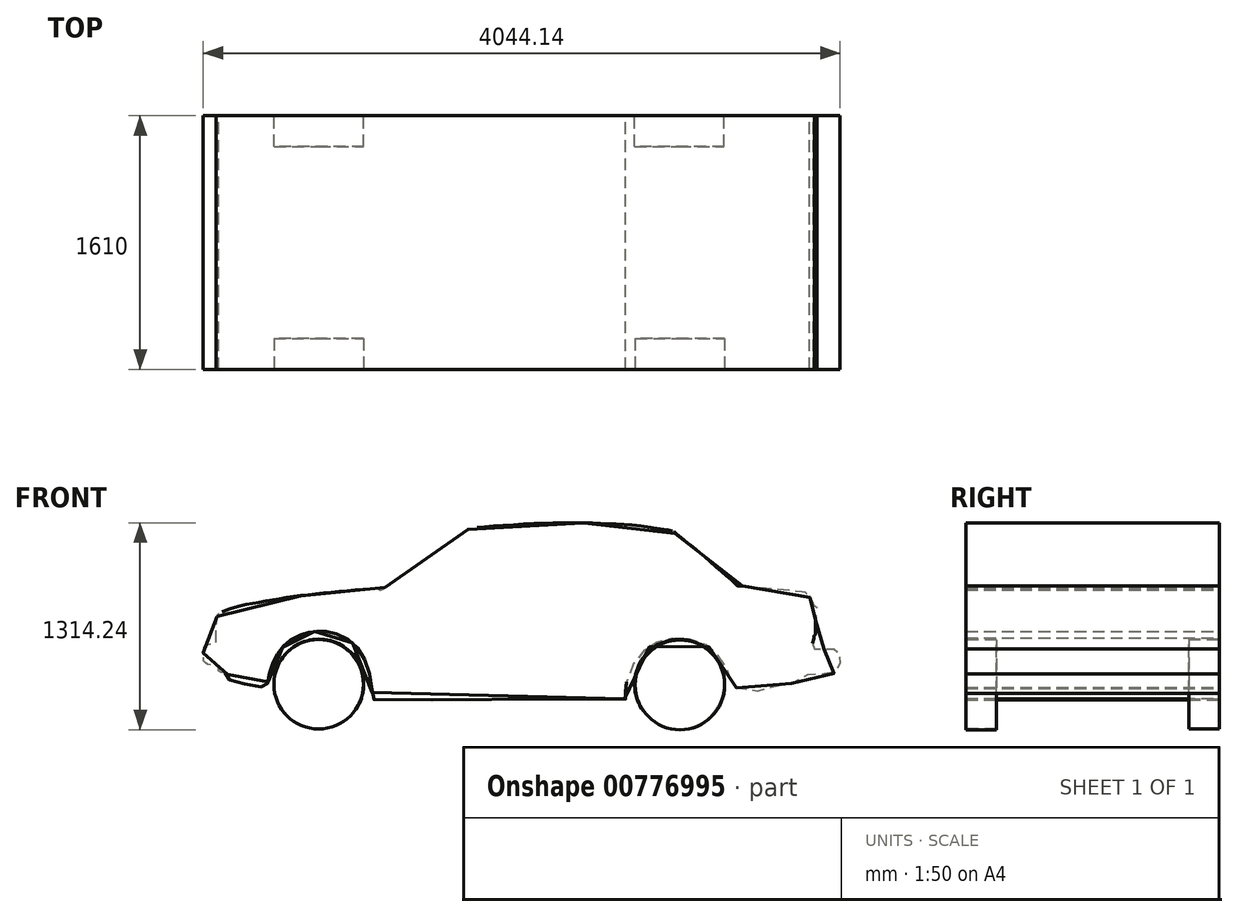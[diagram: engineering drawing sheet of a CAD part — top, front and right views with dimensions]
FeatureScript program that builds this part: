
annotation { "Feature Type Name" : "Feature", "Feature Type Description" : "" }
export const myFeature = defineFeature(function(context is Context, id is Id, definition is map)
    precondition{}
    {
        {
            var Q0;
            Q0=qCreatedBy(makeId("Front.planeOp"),FACE);
            var sketch = newSketch(context, id + "F0", { "sketchPlane" : qUnion([Q0])});
            skLineSegment(sketch, "E0", {"start": v(-4800.55, 868.38) * mm, "end": v(-4800.55, 1009.53) * mm, "construction": true});
            skFitSpline(sketch, "E1", {"points": [v(-2124.67, 593.9) * mm, v(-3714.16, 588.78) * mm, v(-3718.32, 591.35) * mm, v(-3722.74, 606.87) * mm, v(-3727.44, 630.77) * mm, v(-3729.78, 647.77) * mm, v(-3738.29, 703.5) * mm, v(-3747.23, 755.84) * mm, v(-3763.82, 814.56) * mm, v(-3776.59, 843.92) * mm, v(-3789.35, 869.45) * mm, v(-3814.84, 907.94) * mm, v(-3841.42, 938.45) * mm, v(-3867.01, 961.1) * mm, v(-3895.56, 980.78) * mm, v(-3929.03, 997.51) * mm, v(-3954.62, 1007.36) * mm, v(-3980.22, 1014.25) * mm, v(-4002.86, 1019.17) * mm, v(-4023.53, 1022.12) * mm, v(-4045.18, 1023.1) * mm, v(-4063.89, 1023.1) * mm, v(-4075.7, 1023.1) * mm, v(-4090.47, 1022.12) * mm, v(-4105.23, 1021.14) * mm, v(-4120.98, 1019.17) * mm, v(-4136.73, 1016.22) * mm, v(-4148.54, 1013.26) * mm, v(-4162.33, 1009.33) * mm, v(-4176.1, 1004.4) * mm, v(-4193.83, 997.51) * mm, v(-4213.51, 988.66) * mm, v(-4243.04, 969.95) * mm, v(-4260.76, 957.16) * mm, v(-4277.5, 943.37) * mm, v(-4292.26, 928.6) * mm, v(-4304.08, 915.81) * mm, v(-4313.92, 903.01) * mm, v(-4321.8, 891.2) * mm, v(-4332.62, 874.47) * mm, v(-4339.51, 862.66) * mm, v(-4349.36, 844.94) * mm, v(-4359.2, 821.31) * mm, v(-4368.06, 797.69) * mm, v(-4375.93, 773.08) * mm, v(-4382.82, 745.51) * mm, v(-4387.75, 720.9) * mm, v(-4390.7, 698.26) * mm, v(-4392.67, 688.42) * mm, v(-4398.57, 675.62) * mm, v(-4404.48, 667.75) * mm, v(-4433.03, 670.7) * mm, v(-4484.22, 677.6) * mm, v(-4554.1, 692.36) * mm, v(-4605.3, 705.16) * mm, v(-4635.8, 715) * mm, v(-4642.7, 725.83) * mm, v(-4647.62, 754.37) * mm, v(-4660.42, 758.31) * mm, v(-4688.97, 764.22) * mm, v(-4700.78, 771.1) * mm, v(-4705.7, 781.94) * mm, v(-4704.72, 794.73) * mm, v(-4704.72, 796.7) * mm, v(-4721.45, 801.62) * mm, v(-4772.64, 813.44) * mm, v(-4783.47, 821.31) * mm, v(-4796.26, 830.17) * mm, v(-4798.23, 841.98) * mm, v(-4801.18, 864.62) * mm, v(-4796.26, 923.69) * mm, v(-4787.4, 933.53) * mm, v(-4763.78, 941.4) * mm, v(-4743.1, 944.36) * mm, v(-4719.48, 946.33) * mm, v(-4719.48, 954.2) * mm, v(-4721.45, 998.5) * mm, v(-4720.47, 1046.73) * mm, v(-4715.54, 1097.92) * mm, v(-4713.58, 1111.7) * mm, v(-4709.64, 1128.44) * mm, v(-4700.78, 1138.28) * mm, v(-4671.25, 1152.06) * mm, v(-4597.42, 1177.66) * mm, v(-4447.8, 1208.17) * mm, v(-4272.57, 1237.7) * mm, v(-4066.84, 1263.3) * mm, v(-3832.56, 1285.94) * mm, v(-3697.7, 1295.78) * mm, v(-3693.76, 1295.78) * mm, v(-3687.86, 1292.83) * mm, v(-3681.95, 1288.89) * mm, v(-3674.07, 1284.95) * mm, v(-3670.14, 1285.94) * mm, v(-3642.57, 1306.6) * mm, v(-3377.78, 1492.66) * mm, v(-3153.34, 1646.22) * mm, v(-3148.42, 1649.17) * mm, v(-3144.48, 1653.1) * mm, v(-3136.6, 1658.03) * mm, v(-3134.64, 1661.97) * mm, v(-3133.65, 1666.89) * mm, v(-3129.72, 1669.84) * mm, v(-3119.87, 1670.83) * mm, v(-3088.37, 1677.72) * mm, v(-2891.5, 1696.42) * mm, v(-2592.25, 1711.19) * mm, v(-2398.32, 1712.17) * mm, v(-2216.22, 1706.26) * mm, v(-2008.51, 1690.51) * mm, v(-1824.43, 1661.97) * mm, v(-1816.56, 1660) * mm, v(-1808.68, 1657.05) * mm, v(-1806.71, 1653.1) * mm, v(-1804.75, 1651.14) * mm, v(-1803.76, 1646.22) * mm, v(-1799.82, 1644.25) * mm, v(-1757.5, 1611.76) * mm, v(-1633.47, 1511.36) * mm, v(-1434.62, 1338.1) * mm, v(-1411, 1315.47) * mm, v(-1409.03, 1311.53) * mm, v(-1403.12, 1311.53) * mm, v(-1346.03, 1307.6) * mm, v(-1275.15, 1301.69) * mm, v(-1117.65, 1289.87) * mm, v(-1028.07, 1280.03) * mm, v(-979.84, 1273.14) * mm, v(-976.89, 1270.19) * mm, v(-970, 1265.26) * mm, v(-950.3, 1241.64) * mm, v(-936.53, 1219) * mm, v(-925.7, 1195.37) * mm, v(-922.75, 1185.53) * mm, v(-916.84, 1184.55) * mm, v(-909.95, 1179.62) * mm, v(-904.04, 1172.73) * mm, v(-903.06, 1167.81) * mm, v(-904.04, 1160.92) * mm, v(-905.03, 1157.97) * mm, v(-907.98, 1153.05) * mm, v(-909.95, 1151.08) * mm, v(-912.9, 1147.14) * mm, v(-915.86, 1144.19) * mm, v(-919.8, 1140.25) * mm, v(-919.8, 1135.33) * mm, v(-914.87, 1125.48) * mm, v(-914.87, 1117.6) * mm, v(-913.89, 1105.8) * mm, v(-912.9, 1083.16) * mm, v(-912.9, 1051.66) * mm, v(-913.89, 1026.06) * mm, v(-915.86, 999.48) * mm, v(-919.8, 997.51) * mm, v(-923.73, 994.56) * mm, v(-923.73, 980.78) * mm, v(-934.56, 942.39) * mm, v(-951.3, 910.89) * mm, v(-950.3, 909.9) * mm, v(-935.54, 909.9) * mm, v(-854.82, 911.87) * mm, v(-788.87, 909.9) * mm, v(-772.14, 906.95) * mm, v(-768.2, 902.03) * mm, v(-763.28, 893.17) * mm, v(-760.32, 882.34) * mm, v(-759.34, 861.67) * mm, v(-757.37, 836.08) * mm, v(-759.34, 822.3) * mm, v(-765.25, 794.73) * mm, v(-773.12, 778) * mm, v(-782.97, 765.2) * mm, v(-800.68, 754.37) * mm, v(-826.28, 754.37) * mm, v(-910.93, 746.5) * mm, v(-947.36, 745.51) * mm, v(-997.56, 742.56) * mm, v(-1000.51, 740.6) * mm, v(-1001.5, 734.69) * mm, v(-1006.42, 723.86) * mm, v(-1015.28, 713.03) * mm, v(-1022.17, 705.16) * mm, v(-1032.01, 699.25) * mm, v(-1063.51, 694.33) * mm, v(-1088.12, 690.39) * mm, v(-1113.72, 685.47) * mm, v(-1254.48, 648.06) * mm, v(-1301.73, 638.22) * mm, v(-1346.03, 632.31) * mm, v(-1363.58, 664.8) * mm, v(-1381.68, 661.84) * mm, v(-1408.13, 664.8) * mm, v(-1427.62, 666.77) * mm, v(-1440.15, 677.6) * mm, v(-1444.32, 694.33) * mm, v(-1455.46, 736.66) * mm, v(-1468, 771.1) * mm, v(-1487.48, 808.51) * mm, v(-1511.15, 844.94) * mm, v(-1541.77, 881.36) * mm, v(-1583.54, 919.75) * mm, v(-1635.04, 950.26) * mm, v(-1697.69, 969.95) * mm, v(-1753.37, 978.81) * mm, v(-1825.76, 978.81) * mm, v(-1885.63, 967) * mm, v(-1927.39, 949.28) * mm, v(-1964.98, 928.6) * mm, v(-2017.88, 886.28) * mm, v(-2051.29, 843.95) * mm, v(-2088.87, 779.97) * mm, v(-2112.54, 701.23) * mm, v(-2119.5, 633.24) * mm, v(-2119.7, 606.35) * mm, v(-2119.17, 593.45) * mm, v(-2124.67, 593.9) * mm]});
            skCircle(sketch, "E2", {"center": v(-1777.61, 688.42) * mm, "radius": 284.4 * mm});
            skCircle(sketch, "E3", {"center": v(-4066.84, 689.6) * mm, "radius": 284.4 * mm});
            skSolve(sketch);
        }
        {
            var Q0;
            Q0=makeQuery(id+"F0.imprint","IMPRINT",FACE,{"disambiguationData":[TD([[makeQuery(id+"F0.imprint","IMPRINT",EDGE,{"derivedFrom":sQuery(id+"F0.wireOp",EDGE,"E1")}),-1.0]])]});
            extrude(context, id + "F1", {"entities" : qUnion([Q0]), "depth" : 1610 * mm, "offsetDistance" : 25 * mm});
        }
        {
            var Q0;
            Q0=makeQuery(id+"F0.imprint","IMPRINT",FACE,{"disambiguationData":[TD([[makeQuery(id+"F0.imprint","IMPRINT",EDGE,{"derivedFrom":sQuery(id+"F0.wireOp",EDGE,"E3")}),1.0]])]});
            var Q1;
            Q1=makeQuery(id+"F0.imprint","IMPRINT",FACE,{"disambiguationData":[TD([[makeQuery(id+"F0.imprint","IMPRINT",EDGE,{"derivedFrom":sQuery(id+"F0.wireOp",EDGE,"E2")}),1.0]])]});
            var Q2;
            Q2=sQuery(id+"F0.wireOp",EDGE,"E2");
            var Q3;
            Q3=sQuery(id+"F0.wireOp",EDGE,"E3");
            extrude(context, id + "F2", {"entities" : qUnion([Q0, Q1]), "surfaceEntities" : qUnion([Q2, Q3]), "depth" : 195 * mm, "offsetDistance" : 25 * mm});
        }
        {
            var Q0;
            Q0=makeQuery(id+"F1.opExtrude","CAP_FACE",FACE,{"disambiguationData":[OSD([sQuery(id+"F0.wireOp",EDGE,"E1")])],"isStart":false});
            cPlane(context, id + "F3", {"entities" : qUnion([Q0]), "cplaneType" : CPlaneType.OFFSET, "offset" : 0 * mm, "width" : 150 * mm, "height" : 150 * mm});
        }
        {
            var Q0;
            Q0=qCreatedBy(id+"F3.planeOp",FACE);
            var sketch = newSketch(context, id + "F4", { "sketchPlane" : qUnion([Q0])});
            skCircle(sketch, "E4", {"center": v(-1773.75, 683.07) * mm, "radius": 284.4 * mm});
            skCircle(sketch, "E5", {"center": v(-4068.43, 687.2) * mm, "radius": 284.4 * mm});
            skSolve(sketch);
        }
        {
            var Q0;
            Q0 = qSketchRegion(id + "F4", true);
            extrude(context, id + "F5", {"entities" : qUnion([Q0]), "oppositeDirection" : true, "depth" : 195 * mm, "offsetDistance" : 25 * mm});
        }
    });
